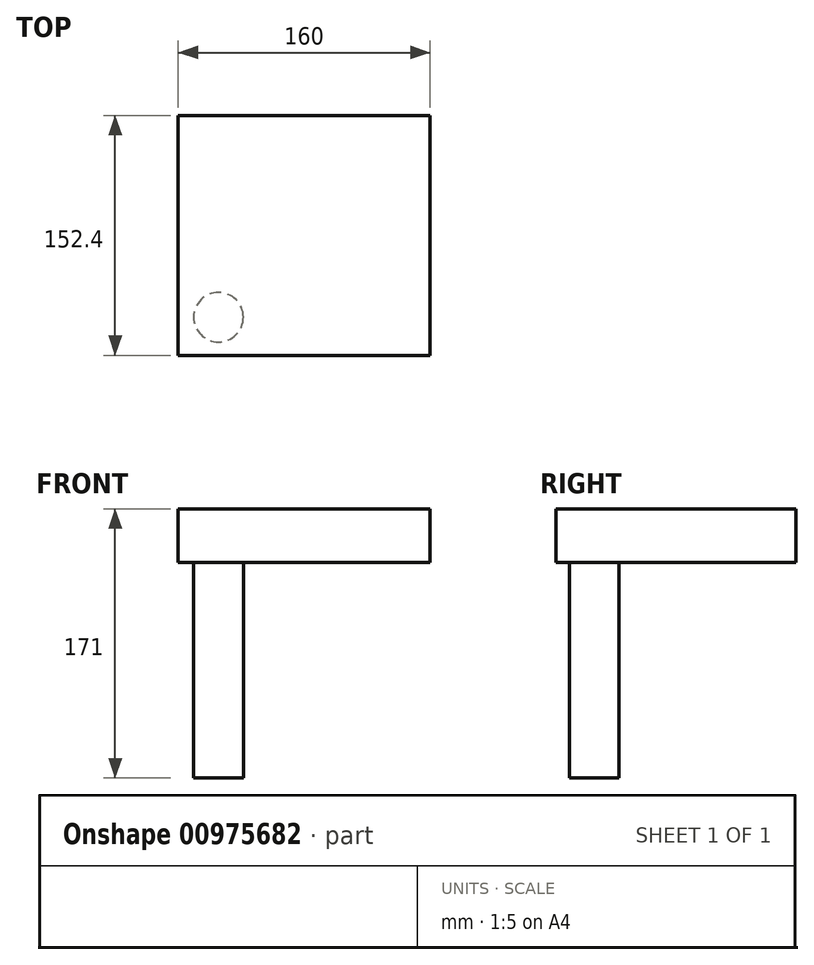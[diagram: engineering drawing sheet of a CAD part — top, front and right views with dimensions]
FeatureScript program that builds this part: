
annotation { "Feature Type Name" : "Feature", "Feature Type Description" : "" }
export const myFeature = defineFeature(function(context is Context, id is Id, definition is map)
    precondition{}
    {
        {
            var Q0;
            Q0=qCreatedBy(makeId("Front.planeOp"),FACE);
            var sketch = newSketch(context, id + "F0", { "sketchPlane" : qUnion([Q0])});
            skLineSegment(sketch, "E0.bottom", {"start": v(-61.6, 34) * mm, "end": v(98.4, 34) * mm});
            skLineSegment(sketch, "E0.top", {"start": v(-61.6, 0) * mm, "end": v(98.4, 0) * mm});
            skLineSegment(sketch, "E0.left", {"start": v(-61.6, 34) * mm, "end": v(-61.6, 0) * mm});
            skLineSegment(sketch, "E0.right", {"start": v(98.4, 34) * mm, "end": v(98.4, 0) * mm});
            skSolve(sketch);
        }
        {
            var Q0;
            Q0 = qSketchRegion(id + "F0", true);
            extrude(context, id + "F1", {"entities" : qUnion([Q0]), "oppositeDirection" : true, "depth" : 152.4 * mm, "offsetDistance" : 25 * mm});
        }
        {
            var Q0;
            Q0=qCreatedBy(makeId("Top.planeOp"),FACE);
            var sketch = newSketch(context, id + "F2", { "sketchPlane" : qUnion([Q0])});
            skCircle(sketch, "E1", {"center": v(-36, 24.26) * mm, "radius": 15.77 * mm});
            skSolve(sketch);
        }
        {
            var Q0;
            Q0 = qSketchRegion(id + "F2", true);
            extrude(context, id + "F3", {"entities" : qUnion([Q0]), "operationType" : NewBodyOperationType.ADD, "oppositeDirection" : true, "depth" : 137 * mm, "offsetDistance" : 25 * mm});
        }
    });
